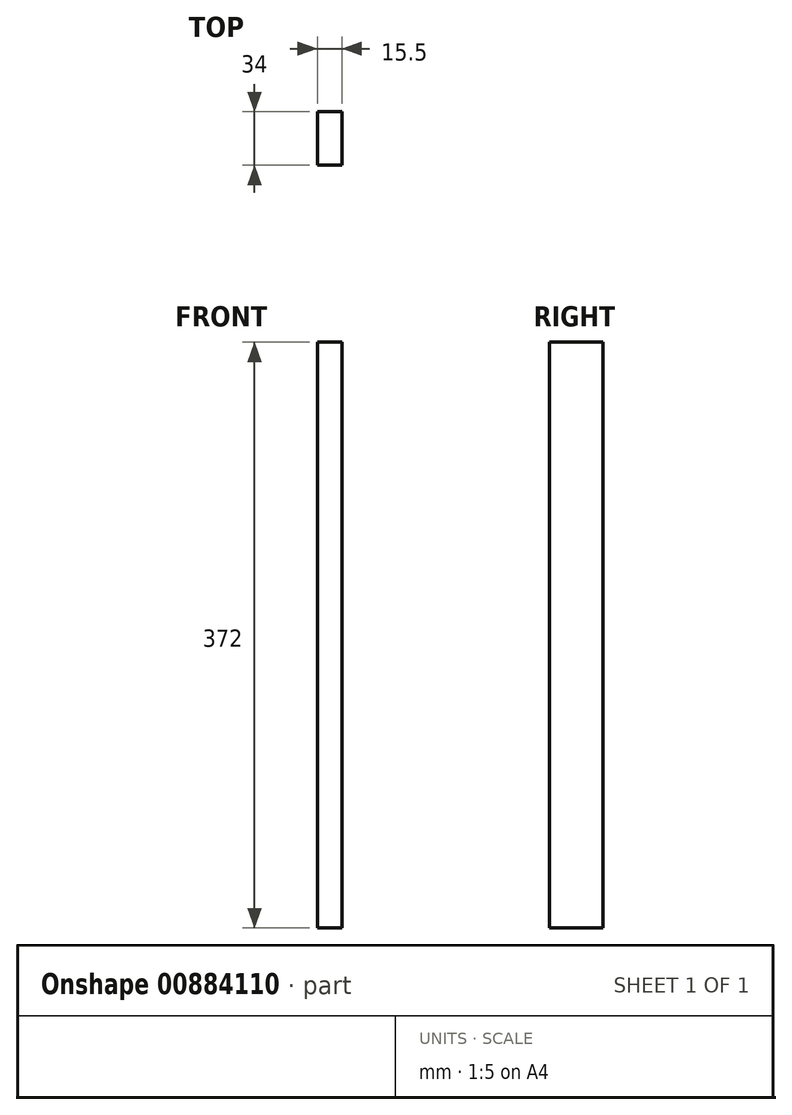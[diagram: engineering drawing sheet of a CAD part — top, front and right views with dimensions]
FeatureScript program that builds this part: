
annotation { "Feature Type Name" : "Feature", "Feature Type Description" : "" }
export const myFeature = defineFeature(function(context is Context, id is Id, definition is map)
    precondition{}
    {
        {
            var Q0;
            Q0=qCreatedBy(makeId("Top.planeOp"),FACE);
            var sketch = newSketch(context, id + "F0", { "sketchPlane" : qUnion([Q0])});
            skLineSegment(sketch, "E0.bottom", {"start": v(0, 0) * mm, "end": v(15.5, 0) * mm});
            skLineSegment(sketch, "E0.top", {"start": v(0, -34) * mm, "end": v(15.5, -34) * mm});
            skLineSegment(sketch, "E0.left", {"start": v(0, 0) * mm, "end": v(0, -34) * mm});
            skLineSegment(sketch, "E0.right", {"start": v(15.5, 0) * mm, "end": v(15.5, -34) * mm});
            skSolve(sketch);
        }
        {
            var Q0;
            Q0=qSketchRegion(id+"F0",true);
            extrude(context, id + "F1", {"entities" : qUnion([Q0]), "depth" : 372 * mm, "offsetDistance" : 25 * mm});
        }
    });
